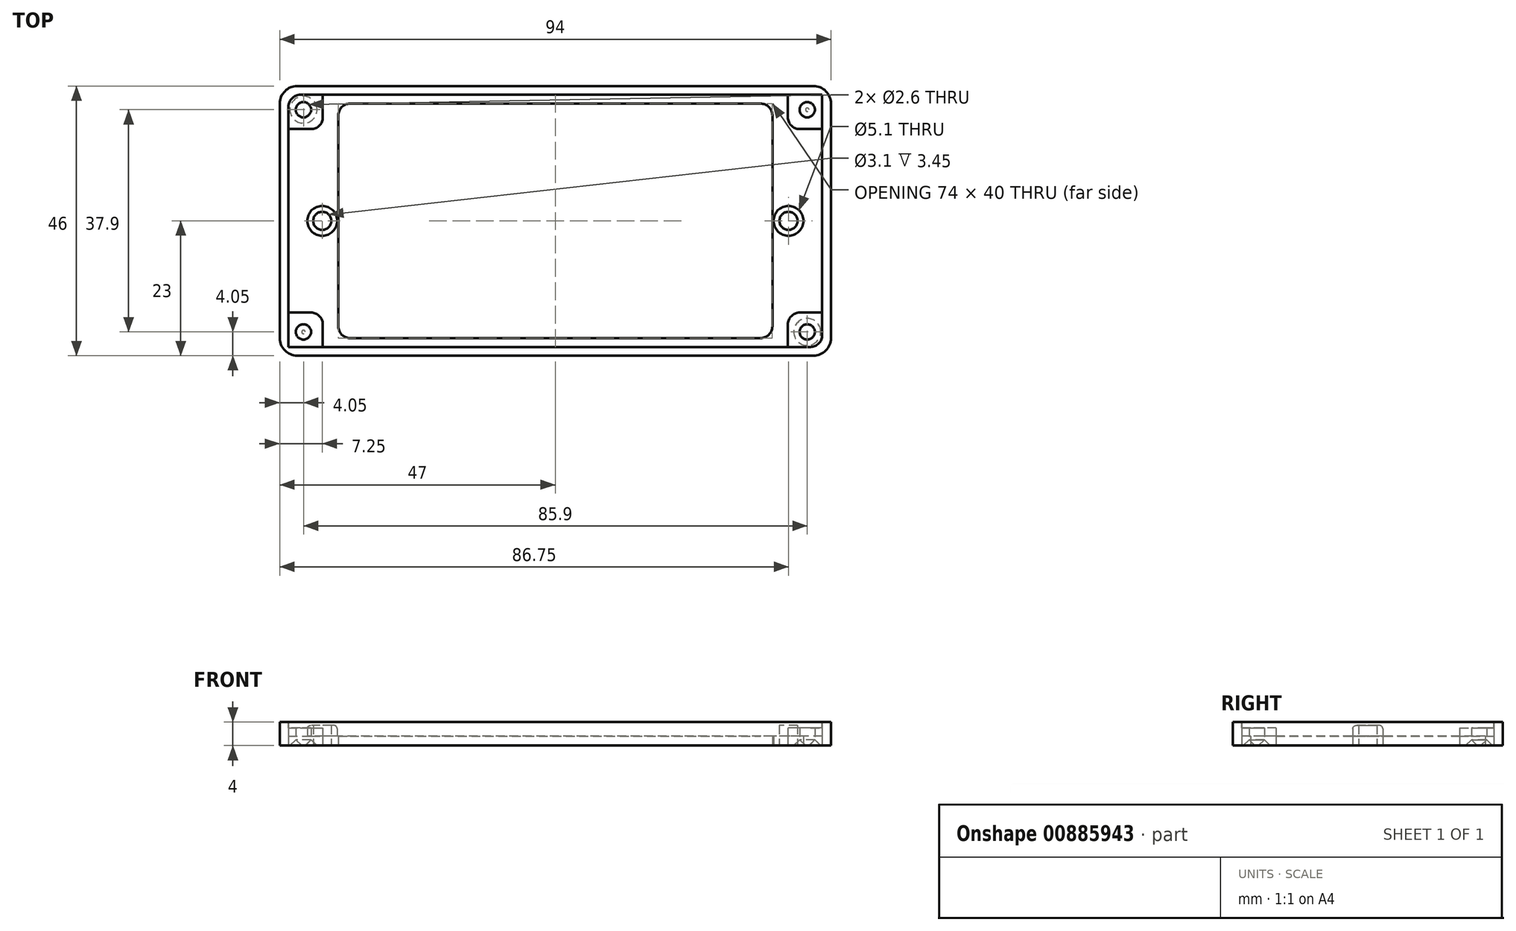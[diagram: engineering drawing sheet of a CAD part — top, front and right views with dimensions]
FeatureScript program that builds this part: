
annotation { "Feature Type Name" : "Feature", "Feature Type Description" : "" }
export const myFeature = defineFeature(function(context is Context, id is Id, definition is map)
    precondition{}
    {
        {
            var Q0;
            Q0=qCreatedBy(makeId("Top.planeOp"),FACE);
            var sketch = newSketch(context, id + "F0", { "sketchPlane" : qUnion([Q0])});
            skLineSegment(sketch, "E0.bottom", {"start": v(-44, 23) * mm, "end": v(44, 23) * mm});
            skLineSegment(sketch, "E0.top", {"start": v(-44, -23) * mm, "end": v(44, -23) * mm});
            skLineSegment(sketch, "E0.left", {"start": v(-47, 20) * mm, "end": v(-47, -20) * mm});
            skLineSegment(sketch, "E0.right", {"start": v(47, 20) * mm, "end": v(47, -20) * mm});
            skPoint(sketch, "E1.visualSharp", {"position": v(-47, 23) * mm});
            skArc(sketch, "E1.filletArc", {"start": v(-44, 23) * mm, "mid": v(-46.12, 22.12) * mm, "end": v(-47, 20) * mm});
            skPoint(sketch, "E2.visualSharp", {"position": v(-47, -23) * mm});
            skArc(sketch, "E2.filletArc", {"start": v(-47, -20) * mm, "mid": v(-46.12, -22.12) * mm, "end": v(-44, -23) * mm});
            skPoint(sketch, "E3.visualSharp", {"position": v(47, -23) * mm});
            skArc(sketch, "E3.filletArc", {"start": v(44, -23) * mm, "mid": v(46.12, -22.12) * mm, "end": v(47, -20) * mm});
            skPoint(sketch, "E4.visualSharp", {"position": v(47, 23) * mm});
            skArc(sketch, "E4.filletArc", {"start": v(47, 20) * mm, "mid": v(46.12, 22.12) * mm, "end": v(44, 23) * mm});
            skLineSegment(sketch, "E5.bottom", {"start": v(-35, 20) * mm, "end": v(35, 20) * mm});
            skLineSegment(sketch, "E5.top", {"start": v(-35, -20) * mm, "end": v(35, -20) * mm});
            skLineSegment(sketch, "E5.left", {"start": v(-37, 18) * mm, "end": v(-37, -18) * mm});
            skLineSegment(sketch, "E5.right", {"start": v(37, 18) * mm, "end": v(37, -18) * mm});
            skCircle(sketch, "E6", {"center": v(-42.95, 18.95) * mm, "radius": 1.3 * mm});
            skCircle(sketch, "E7.MirrorC", {"center": v(-42.95, -18.95) * mm, "radius": 1.3 * mm});
            skCircle(sketch, "E8.MirrorC", {"center": v(42.95, 18.95) * mm, "radius": 1.3 * mm});
            skCircle(sketch, "E9.MirrorC", {"center": v(42.95, -18.95) * mm, "radius": 1.3 * mm});
            skCircle(sketch, "E10", {"center": v(-39.75, 0) * mm, "radius": 1.55 * mm});
            skCircle(sketch, "E11.MirrorC", {"center": v(39.75, 0) * mm, "radius": 1.55 * mm});
            skCircle(sketch, "E12", {"center": v(-39.75, 0) * mm, "radius": 2.55 * mm});
            skCircle(sketch, "E13.MirrorC", {"center": v(39.75, 0) * mm, "radius": 2.55 * mm});
            skLineSegment(sketch, "E14.bottom", {"start": v(-47, 15.65) * mm, "end": v(-41.65, 15.65) * mm});
            skLineSegment(sketch, "E14.top", {"start": v(-44, 23) * mm, "end": v(-39.65, 23) * mm});
            skLineSegment(sketch, "E14.left", {"start": v(-47, 15.65) * mm, "end": v(-47, 20) * mm});
            skLineSegment(sketch, "E14.right", {"start": v(-39.65, 17.65) * mm, "end": v(-39.65, 23) * mm});
            skPoint(sketch, "E15.visualSharp", {"position": v(-39.65, 15.65) * mm});
            skArc(sketch, "E15.filletArc", {"start": v(-41.65, 15.65) * mm, "mid": v(-40.24, 16.24) * mm, "end": v(-39.65, 17.65) * mm});
            skLineSegment(sketch, "E16.MirrorCS", {"start": v(-47, -15.65) * mm, "end": v(-41.65, -15.65) * mm});
            skArc(sketch, "E17.MirrorCS", {"start": v(-41.65, -15.65) * mm, "mid": v(-40.24, -16.24) * mm, "end": v(-39.65, -17.65) * mm});
            skLineSegment(sketch, "E18.MirrorCS", {"start": v(-39.65, -17.65) * mm, "end": v(-39.65, -23) * mm});
            skLineSegment(sketch, "E19.MirrorCS", {"start": v(39.65, 17.65) * mm, "end": v(39.65, 23) * mm});
            skLineSegment(sketch, "E20.MirrorCS", {"start": v(47, 15.65) * mm, "end": v(41.65, 15.65) * mm});
            skLineSegment(sketch, "E21.MirrorCS", {"start": v(47, -15.65) * mm, "end": v(41.65, -15.65) * mm});
            skLineSegment(sketch, "E22.MirrorCS", {"start": v(39.65, -17.65) * mm, "end": v(39.65, -23) * mm});
            skArc(sketch, "E23.MirrorCS", {"start": v(41.65, -15.65) * mm, "mid": v(40.24, -16.24) * mm, "end": v(39.65, -17.65) * mm});
            skArc(sketch, "E24.MirrorCS", {"start": v(41.65, 15.65) * mm, "mid": v(40.24, 16.24) * mm, "end": v(39.65, 17.65) * mm});
            skPoint(sketch, "E25.visualSharp", {"position": v(-37, 20) * mm});
            skArc(sketch, "E25.filletArc", {"start": v(-35, 20) * mm, "mid": v(-36.41, 19.41) * mm, "end": v(-37, 18) * mm});
            skPoint(sketch, "E26.visualSharp", {"position": v(-37, -20) * mm});
            skArc(sketch, "E26.filletArc", {"start": v(-37, -18) * mm, "mid": v(-36.41, -19.41) * mm, "end": v(-35, -20) * mm});
            skPoint(sketch, "E27.visualSharp", {"position": v(37, -20) * mm});
            skArc(sketch, "E27.filletArc", {"start": v(35, -20) * mm, "mid": v(36.41, -19.41) * mm, "end": v(37, -18) * mm});
            skPoint(sketch, "E28.visualSharp", {"position": v(37, 20) * mm});
            skArc(sketch, "E28.filletArc", {"start": v(37, 18) * mm, "mid": v(36.41, 19.41) * mm, "end": v(35, 20) * mm});
            skLineSegment(sketch, "E29.bottom", {"start": v(45.5, -21.5) * mm, "end": v(-45.5, -21.5) * mm});
            skLineSegment(sketch, "E29.top", {"start": v(45.5, 21.5) * mm, "end": v(-45.5, 21.5) * mm});
            skLineSegment(sketch, "E29.left", {"start": v(45.5, -21.5) * mm, "end": v(45.5, 21.5) * mm});
            skLineSegment(sketch, "E29.right", {"start": v(-45.5, -21.5) * mm, "end": v(-45.5, 21.5) * mm});
            skSolve(sketch);
        }
        {
            var Q0;
            {var subQ1=sQuery(id+"F0.wireOp",EDGE,"E0.left");var subQ3=sQuery(id+"F0.wireOp",EDGE,"E16.MirrorCS");var subQ4=makeQuery(id+"F0.imprint","INTERSECT",VERTEX,{"derivedFrom":[subQ1,subQ3]});Q0=makeQuery(id+"F0.imprint","IMPRINT",FACE,{"disambiguationData":[TD([[makeQuery(id+"F0.imprint","IMPRINT",EDGE,{"disambiguationData":[TD([[subQ4,-1.0]])],"derivedFrom":subQ3}),1.0]])]});}
            var Q1;
            {var subQ5=sQuery(id+"F0.wireOp",EDGE,"E2.filletArc");Q1=makeQuery(id+"F0.imprint","IMPRINT",FACE,{"disambiguationData":[TD([[makeQuery(id+"F0.imprint","IMPRINT",EDGE,{"derivedFrom":subQ5}),1.0]])]});}
            var Q2;
            Q2=makeQuery(id+"F0.imprint","IMPRINT",FACE,{"disambiguationData":[TD([[makeQuery(id+"F0.imprint","IMPRINT",EDGE,{"derivedFrom":sQuery(id+"F0.wireOp",EDGE,"E7.MirrorC")}),1.0]])]});
            var Q3;
            {var subQ0=sQuery(id+"F0.wireOp",EDGE,"E18.MirrorCS");var subQ1=sQuery(id+"F0.wireOp",EDGE,"E0.top");var subQ2=makeQuery(id+"F0.imprint","INTERSECT",VERTEX,{"derivedFrom":[subQ1,subQ0]});Q3=makeQuery(id+"F0.imprint","IMPRINT",FACE,{"disambiguationData":[TD([[makeQuery(id+"F0.imprint","IMPRINT",EDGE,{"disambiguationData":[TD([[subQ2,-1.0]])],"derivedFrom":subQ1}),1.0]])]});}
            var Q4;
            Q4=makeQuery(id+"F0.imprint","IMPRINT",FACE,{"disambiguationData":[TD([[makeQuery(id+"F0.imprint","IMPRINT",EDGE,{"derivedFrom":sQuery(id+"F0.wireOp",EDGE,"E1.filletArc")}),1.0]])]});
            var Q5;
            Q5=makeQuery(id+"F0.imprint","IMPRINT",FACE,{"disambiguationData":[TD([[makeQuery(id+"F0.imprint","IMPRINT",EDGE,{"derivedFrom":sQuery(id+"F0.wireOp",EDGE,"E6")}),-1.0]])]});
            var Q6;
            {var subQ1=sQuery(id+"F0.wireOp",EDGE,"E0.bottom");var subQ3=sQuery(id+"F0.wireOp",EDGE,"E19.MirrorCS");var subQ4=makeQuery(id+"F0.imprint","INTERSECT",VERTEX,{"derivedFrom":[subQ1,subQ3]});Q6=makeQuery(id+"F0.imprint","IMPRINT",FACE,{"disambiguationData":[TD([[makeQuery(id+"F0.imprint","IMPRINT",EDGE,{"disambiguationData":[TD([[subQ4,1.0]])],"derivedFrom":subQ3}),1.0]])]});}
            var Q7;
            {var subQ5=sQuery(id+"F0.wireOp",EDGE,"E4.filletArc");Q7=makeQuery(id+"F0.imprint","IMPRINT",FACE,{"disambiguationData":[TD([[makeQuery(id+"F0.imprint","IMPRINT",EDGE,{"derivedFrom":subQ5}),1.0]])]});}
            var Q8;
            Q8=makeQuery(id+"F0.imprint","IMPRINT",FACE,{"disambiguationData":[TD([[makeQuery(id+"F0.imprint","IMPRINT",EDGE,{"derivedFrom":sQuery(id+"F0.wireOp",EDGE,"E8.MirrorC")}),1.0]])]});
            var Q9;
            Q9=makeQuery(id+"F0.imprint","IMPRINT",FACE,{"disambiguationData":[TD([[makeQuery(id+"F0.imprint","IMPRINT",EDGE,{"derivedFrom":sQuery(id+"F0.wireOp",EDGE,"E9.MirrorC")}),-1.0]])]});
            var Q10;
            {var subQ5=sQuery(id+"F0.wireOp",EDGE,"E3.filletArc");Q10=makeQuery(id+"F0.imprint","IMPRINT",FACE,{"disambiguationData":[TD([[makeQuery(id+"F0.imprint","IMPRINT",EDGE,{"derivedFrom":subQ5}),1.0]])]});}
            var Q11;
            {var subQ0=sQuery(id+"F0.wireOp",EDGE,"E20.MirrorCS");var subQ1=sQuery(id+"F0.wireOp",EDGE,"E0.right");var subQ2=makeQuery(id+"F0.imprint","INTERSECT",VERTEX,{"derivedFrom":[subQ1,subQ0]});Q11=makeQuery(id+"F0.imprint","IMPRINT",FACE,{"disambiguationData":[TD([[makeQuery(id+"F0.imprint","IMPRINT",EDGE,{"disambiguationData":[TD([[subQ2,-1.0]])],"derivedFrom":subQ1}),-1.0]])]});}
            extrude(context, id + "F1", {"entities" : qUnion([Q0, Q1, Q2, Q3, Q4, Q5, Q6, Q7, Q8, Q9, Q10, Q11]), "depth" : 4 * mm, "offsetDistance" : 25 * mm});
        }
        {
            var Q0;
            Q0=makeQuery(id+"F0.imprint","IMPRINT",FACE,{"disambiguationData":[TD([[makeQuery(id+"F0.imprint","IMPRINT",EDGE,{"derivedFrom":sQuery(id+"F0.wireOp",EDGE,"E5.bottom")}),1.0]])]});
            extrude(context, id + "F2", {"entities" : qUnion([Q0]), "operationType" : NewBodyOperationType.ADD, "depth" : 1.6 * mm, "offsetDistance" : 25 * mm});
        }
        {
            var Q0;
            Q0=makeQuery(id+"F0.imprint","IMPRINT",FACE,{"disambiguationData":[TD([[makeQuery(id+"F0.imprint","IMPRINT",EDGE,{"derivedFrom":sQuery(id+"F0.wireOp",EDGE,"E10")}),-1.0]])]});
            var Q1;
            Q1=makeQuery(id+"F0.imprint","IMPRINT",FACE,{"disambiguationData":[TD([[makeQuery(id+"F0.imprint","IMPRINT",EDGE,{"derivedFrom":sQuery(id+"F0.wireOp",EDGE,"E11.MirrorC")}),1.0]])]});
            extrude(context, id + "F3", {"entities" : qUnion([Q0, Q1]), "operationType" : NewBodyOperationType.ADD, "depth" : 3.45 * mm, "offsetDistance" : 25 * mm});
        }
        {
            var Q0;
            Q0=makeQuery(id+"F1.opExtrude","CAP_FACE",FACE,{"disambiguationData":[OSD([sQuery(id+"F0.wireOp",EDGE,"E0.bottom"),sQuery(id+"F0.wireOp",EDGE,"E0.top"),sQuery(id+"F0.wireOp",EDGE,"E0.left"),sQuery(id+"F0.wireOp",EDGE,"E0.right"),sQuery(id+"F0.wireOp",EDGE,"E1.filletArc"),sQuery(id+"F0.wireOp",EDGE,"E2.filletArc"),sQuery(id+"F0.wireOp",EDGE,"E3.filletArc"),sQuery(id+"F0.wireOp",EDGE,"E4.filletArc"),sQuery(id+"F0.wireOp",EDGE,"E6"),sQuery(id+"F0.wireOp",EDGE,"E7.MirrorC"),sQuery(id+"F0.wireOp",EDGE,"E8.MirrorC"),sQuery(id+"F0.wireOp",EDGE,"E9.MirrorC"),sQuery(id+"F0.wireOp",EDGE,"E14.bottom"),sQuery(id+"F0.wireOp",EDGE,"E14.top"),sQuery(id+"F0.wireOp",EDGE,"E14.left"),sQuery(id+"F0.wireOp",EDGE,"E14.right"),sQuery(id+"F0.wireOp",EDGE,"E15.filletArc"),sQuery(id+"F0.wireOp",EDGE,"E16.MirrorCS"),sQuery(id+"F0.wireOp",EDGE,"E17.MirrorCS"),sQuery(id+"F0.wireOp",EDGE,"E18.MirrorCS"),sQuery(id+"F0.wireOp",EDGE,"E19.MirrorCS"),sQuery(id+"F0.wireOp",EDGE,"E20.MirrorCS"),sQuery(id+"F0.wireOp",EDGE,"E21.MirrorCS"),sQuery(id+"F0.wireOp",EDGE,"E22.MirrorCS"),sQuery(id+"F0.wireOp",EDGE,"E23.MirrorCS"),sQuery(id+"F0.wireOp",EDGE,"E24.MirrorCS"),sQuery(id+"F0.wireOp",EDGE,"E29.bottom"),sQuery(id+"F0.wireOp",EDGE,"E29.top"),sQuery(id+"F0.wireOp",EDGE,"E29.left"),sQuery(id+"F0.wireOp",EDGE,"E29.right")])],"isStart":false});
            var sketch = newSketch(context, id + "F4", { "sketchPlane" : qUnion([Q0])});
            skLineSegment(sketch, "E30.bottom", {"start": v(-45.5, 15.65) * mm, "end": v(-41.65, 15.65) * mm});
            skLineSegment(sketch, "E30.top", {"start": v(-43.5, 21.5) * mm, "end": v(-39.65, 21.5) * mm});
            skLineSegment(sketch, "E30.left", {"start": v(-45.5, 15.65) * mm, "end": v(-45.5, 19.5) * mm});
            skLineSegment(sketch, "E30.right", {"start": v(-39.65, 17.65) * mm, "end": v(-39.65, 21.5) * mm});
            skPoint(sketch, "E31.visualSharp", {"position": v(-45.5, 21.5) * mm});
            skArc(sketch, "E31.filletArc", {"start": v(-43.5, 21.5) * mm, "mid": v(-44.91, 20.91) * mm, "end": v(-45.5, 19.5) * mm});
            skPoint(sketch, "E32.visualSharp", {"position": v(-39.65, 15.65) * mm});
            skArc(sketch, "E32.filletArc", {"start": v(-41.65, 15.65) * mm, "mid": v(-40.24, 16.24) * mm, "end": v(-39.65, 17.65) * mm});
            skLineSegment(sketch, "E33.MirrorCS", {"start": v(-45.5, -15.65) * mm, "end": v(-41.65, -15.65) * mm});
            skLineSegment(sketch, "E34.MirrorCS", {"start": v(-45.5, -15.65) * mm, "end": v(-45.5, -19.5) * mm});
            skLineSegment(sketch, "E35.MirrorCS", {"start": v(-43.5, -21.5) * mm, "end": v(-39.65, -21.5) * mm});
            skLineSegment(sketch, "E36.MirrorCS", {"start": v(-39.65, -17.65) * mm, "end": v(-39.65, -21.5) * mm});
            skArc(sketch, "E37.MirrorCS", {"start": v(-41.65, -15.65) * mm, "mid": v(-40.24, -16.24) * mm, "end": v(-39.65, -17.65) * mm});
            skArc(sketch, "E38.MirrorCS", {"start": v(-43.5, -21.5) * mm, "mid": v(-44.91, -20.91) * mm, "end": v(-45.5, -19.5) * mm});
            skLineSegment(sketch, "E39.MirrorCS", {"start": v(39.65, -17.65) * mm, "end": v(39.65, -21.5) * mm});
            skLineSegment(sketch, "E40.MirrorCS", {"start": v(43.5, -21.5) * mm, "end": v(39.65, -21.5) * mm});
            skArc(sketch, "E41.MirrorCS", {"start": v(43.5, -21.5) * mm, "mid": v(44.91, -20.91) * mm, "end": v(45.5, -19.5) * mm});
            skLineSegment(sketch, "E42.MirrorCS", {"start": v(45.5, -15.65) * mm, "end": v(45.5, -19.5) * mm});
            skLineSegment(sketch, "E43.MirrorCS", {"start": v(45.5, -15.65) * mm, "end": v(41.65, -15.65) * mm});
            skArc(sketch, "E44.MirrorCS", {"start": v(41.65, -15.65) * mm, "mid": v(40.24, -16.24) * mm, "end": v(39.65, -17.65) * mm});
            skLineSegment(sketch, "E45.MirrorCS", {"start": v(45.5, 15.65) * mm, "end": v(41.65, 15.65) * mm});
            skLineSegment(sketch, "E46.MirrorCS", {"start": v(45.5, 15.65) * mm, "end": v(45.5, 19.5) * mm});
            skArc(sketch, "E47.MirrorCS", {"start": v(43.5, 21.5) * mm, "mid": v(44.91, 20.91) * mm, "end": v(45.5, 19.5) * mm});
            skLineSegment(sketch, "E48.MirrorCS", {"start": v(43.5, 21.5) * mm, "end": v(39.65, 21.5) * mm});
            skLineSegment(sketch, "E49.MirrorCS", {"start": v(39.65, 17.65) * mm, "end": v(39.65, 21.5) * mm});
            skArc(sketch, "E50.MirrorCS", {"start": v(41.65, 15.65) * mm, "mid": v(40.24, 16.24) * mm, "end": v(39.65, 17.65) * mm});
            skSolve(sketch);
        }
        {
            var Q0;
            Q0=makeQuery(id+"F4.imprint","IMPRINT",FACE,{"disambiguationData":[TD([[makeQuery(id+"F4.imprint","IMPRINT",EDGE,{"derivedFrom":sQuery(id+"F4.wireOp",EDGE,"E30.bottom")}),1.0]])]});
            var Q1;
            Q1=makeQuery(id+"F4.imprint","IMPRINT",FACE,{"disambiguationData":[TD([[makeQuery(id+"F4.imprint","IMPRINT",EDGE,{"derivedFrom":sQuery(id+"F4.wireOp",EDGE,"E33.MirrorCS")}),-1.0]])]});
            var Q2;
            Q2=makeQuery(id+"F4.imprint","IMPRINT",FACE,{"disambiguationData":[TD([[makeQuery(id+"F4.imprint","IMPRINT",EDGE,{"derivedFrom":sQuery(id+"F4.wireOp",EDGE,"E39.MirrorCS")}),1.0]])]});
            var Q3;
            Q3=makeQuery(id+"F4.imprint","IMPRINT",FACE,{"disambiguationData":[TD([[makeQuery(id+"F4.imprint","IMPRINT",EDGE,{"derivedFrom":sQuery(id+"F4.wireOp",EDGE,"E45.MirrorCS")}),-1.0]])]});
            extrude(context, id + "F5", {"entities" : qUnion([Q0, Q1, Q2, Q3]), "operationType" : NewBodyOperationType.REMOVE, "oppositeDirection" : true, "depth" : 1 * mm, "offsetDistance" : 25 * mm});
        }
        {
            var Q0;
            Q0=makeQuery(id+"F1.opExtrude","CAP_EDGE",EDGE,{"disambiguationData":[OSD([sQuery(id+"F0.wireOp",EDGE,"E8.MirrorC")])],"isStart":true});
            var Q1;
            Q1=makeQuery(id+"F1.opExtrude","CAP_EDGE",EDGE,{"disambiguationData":[OSD([sQuery(id+"F0.wireOp",EDGE,"E9.MirrorC")])],"isStart":true});
            var Q2;
            Q2=makeQuery(id+"F1.opExtrude","CAP_EDGE",EDGE,{"disambiguationData":[OSD([sQuery(id+"F0.wireOp",EDGE,"E7.MirrorC")])],"isStart":true});
            var Q3;
            Q3=makeQuery(id+"F1.opExtrude","CAP_EDGE",EDGE,{"disambiguationData":[OSD([sQuery(id+"F0.wireOp",EDGE,"E6")])],"isStart":true});
            chamfer(context, id + "F6", {"entities" : qUnion([Q0, Q1, Q2, Q3]), "width" : 1 * mm, "tangentPropagation" : true});
        }
        {
            var Q0;
            Q0=makeQuery(id+"F3.opExtrude","CAP_EDGE",EDGE,{"disambiguationData":[OSD([sQuery(id+"F0.wireOp",EDGE,"E13.MirrorC")])],"isStart":false});
            var Q1;
            Q1=makeQuery(id+"F3.opExtrude","CAP_EDGE",EDGE,{"disambiguationData":[OSD([sQuery(id+"F0.wireOp",EDGE,"E12")])],"isStart":false});
            fillet(context, id + "F7", {"entities" : qUnion([Q0, Q1]), "radius" : 0.6 * mm, "tangentPropagation" : true, "allowEdgeOverflow" : false});
        }
    });
